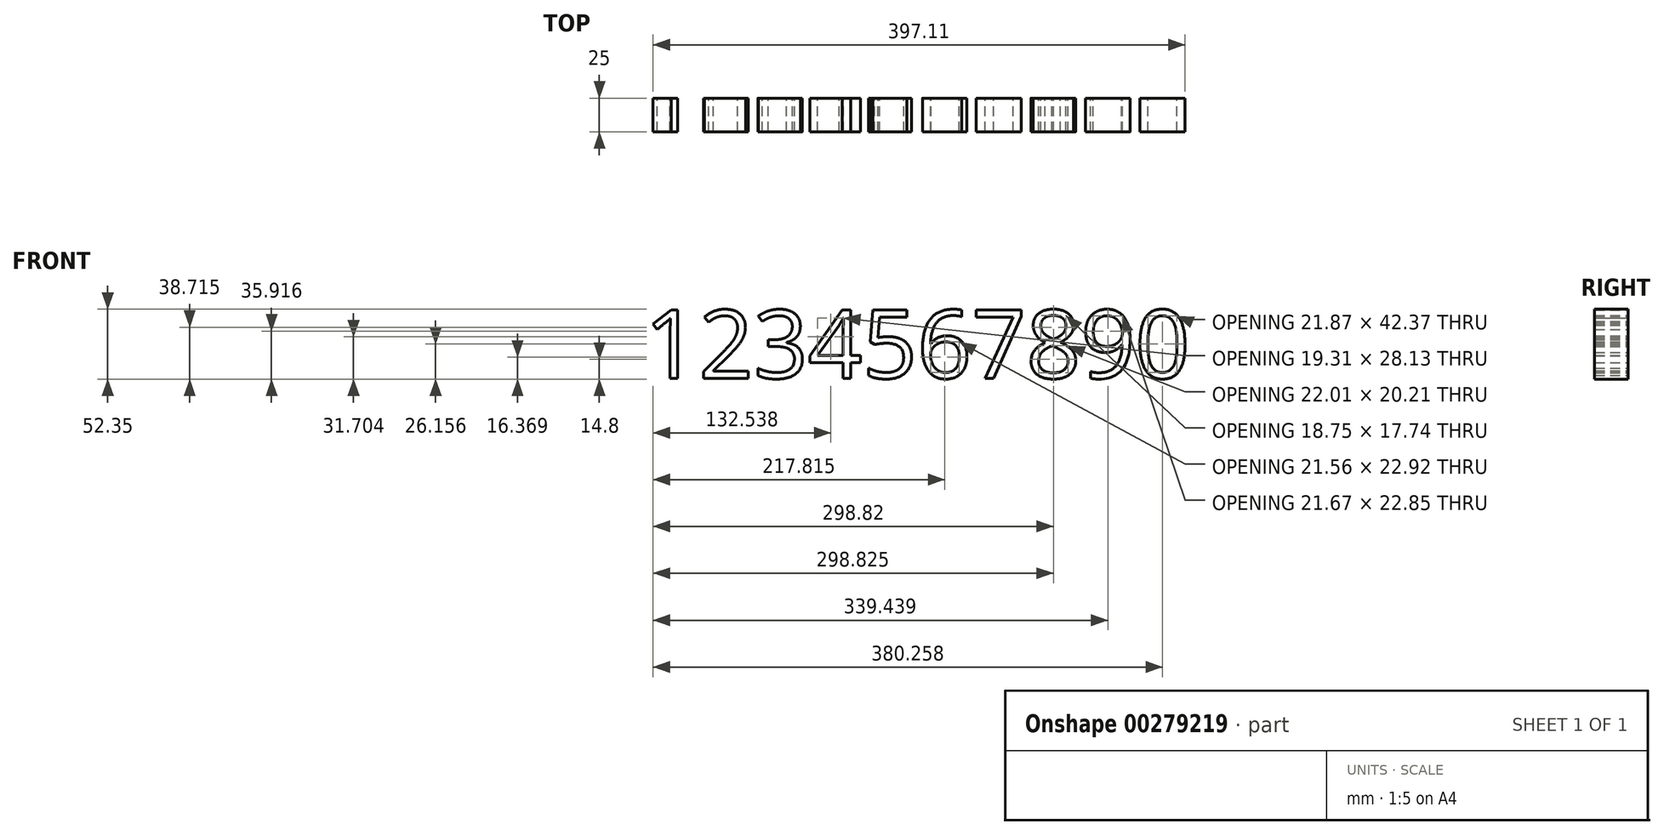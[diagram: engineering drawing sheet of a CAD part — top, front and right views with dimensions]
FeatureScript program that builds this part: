
annotation { "Feature Type Name" : "Feature", "Feature Type Description" : "" }
export const myFeature = defineFeature(function(context is Context, id is Id, definition is map)
    precondition{}
    {
        {
            var Q0;
            Q0=qCreatedBy(makeId("Front.planeOp"),FACE);
            var sketch = newSketch(context, id + "F0", { "sketchPlane" : qUnion([Q0])});
            skText(sketch, "E0", { "text": "1234567890", "fontName": "OpenSans-Regular.ttf"});
            const initialGuessF0  = {"E0": [-0.14938, -0.08854, 1, 0, 0.05128]};
            skSetInitialGuess(sketch, initialGuessF0);
            skSolve(sketch);
        }
        {
            var Q0;
            Q0 = qSketchRegion(id + "F0", true);
            extrude(context, id + "F1", {"entities" : qUnion([Q0]), "depth" : 25 * mm});
        }
    });
